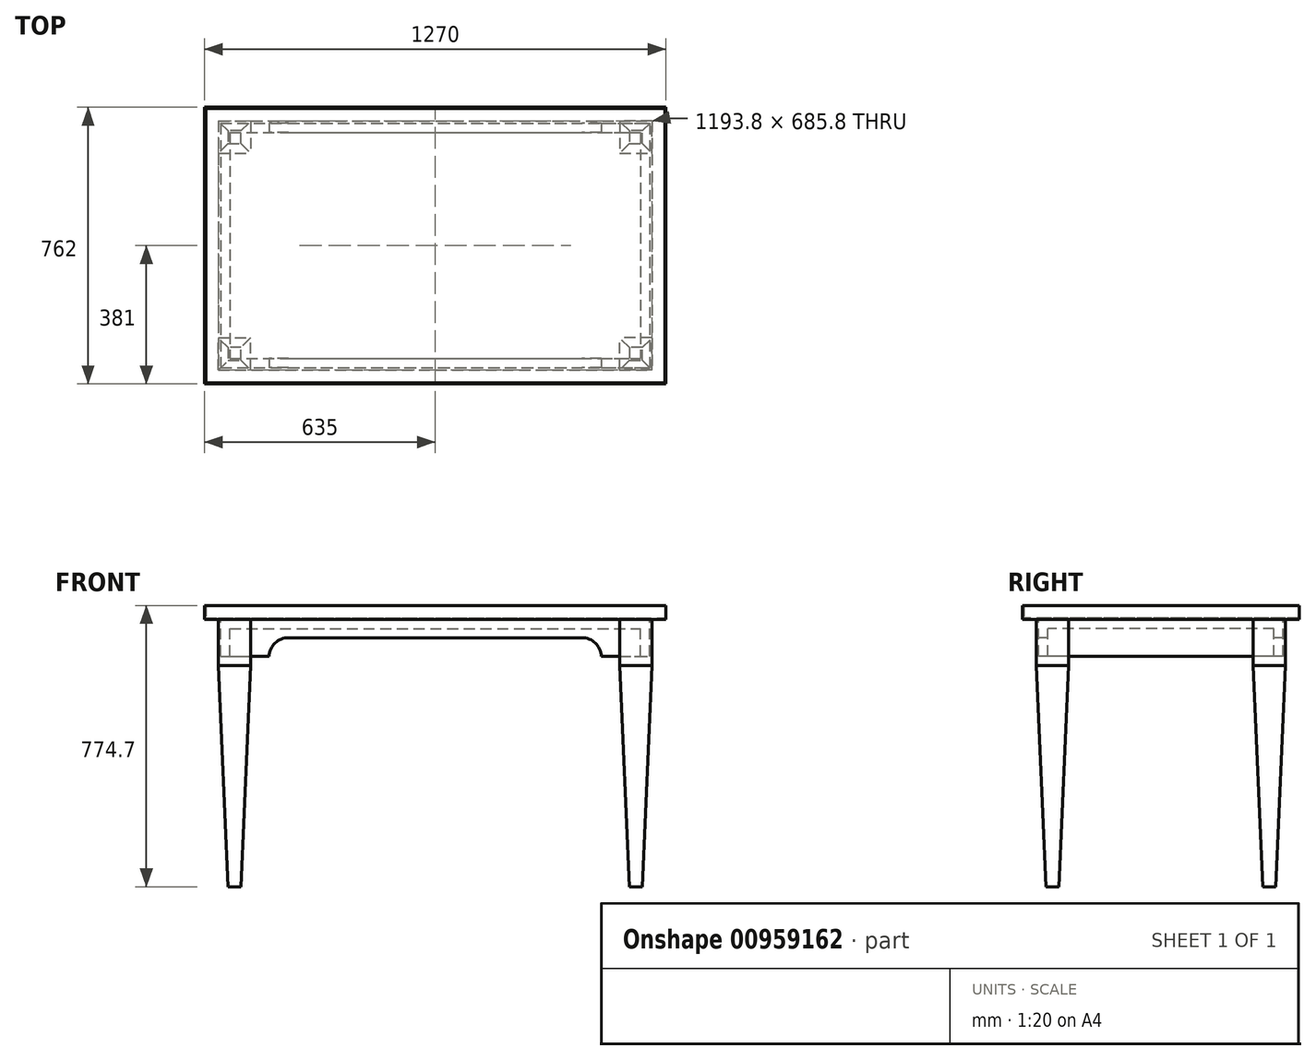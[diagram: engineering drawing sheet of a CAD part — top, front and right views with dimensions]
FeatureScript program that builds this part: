
annotation { "Feature Type Name" : "Feature", "Feature Type Description" : "" }
export const myFeature = defineFeature(function(context is Context, id is Id, definition is map)
    precondition{}
    {
        {
            var Q0;
            Q0=qCreatedBy(makeId("Top.planeOp"),FACE);
            var sketch = newSketch(context, id + "F0", { "sketchPlane" : qUnion([Q0])});
            skLineSegment(sketch, "E0.bottom", {"start": v(-635, 381) * mm, "end": v(635, 381) * mm});
            skLineSegment(sketch, "E0.top", {"start": v(-635, -381) * mm, "end": v(635, -381) * mm});
            skLineSegment(sketch, "E0.left", {"start": v(-635, 381) * mm, "end": v(-635, -381) * mm});
            skLineSegment(sketch, "E0.right", {"start": v(635, 381) * mm, "end": v(635, -381) * mm});
            skPoint(sketch, "E0.middle", {"position": v(0, 0) * mm});
            skLineSegment(sketch, "E1.0", {"start": v(-631.82, 377.83) * mm, "end": v(631.83, 377.83) * mm});
            skLineSegment(sketch, "E1.1", {"start": v(-631.82, 377.83) * mm, "end": v(-631.83, -377.82) * mm});
            skLineSegment(sketch, "E1.2", {"start": v(-631.83, -377.82) * mm, "end": v(631.82, -377.82) * mm});
            skLineSegment(sketch, "E1.3", {"start": v(631.83, 377.83) * mm, "end": v(631.82, -377.82) * mm});
            skLineSegment(sketch, "E2.0", {"start": v(-596.9, 342.9) * mm, "end": v(596.9, 342.9) * mm});
            skLineSegment(sketch, "E2.1", {"start": v(-596.9, 342.9) * mm, "end": v(-596.9, -342.9) * mm});
            skLineSegment(sketch, "E2.2", {"start": v(-596.9, -342.9) * mm, "end": v(596.9, -342.9) * mm});
            skLineSegment(sketch, "E2.3", {"start": v(596.9, 342.9) * mm, "end": v(596.9, -342.9) * mm});
            skSolve(sketch);
        }
        {
            var Q0;
            Q0=qSketchRegion(id+"F0",true);
            extrude(context, id + "F1", {"entities" : qUnion([Q0]), "depth" : 38.1 * mm, "offsetDistance" : 25.4 * mm});
        }
        {
            var Q0;
            Q0=makeQuery(id+"F1.opExtrude","CAP_FACE",FACE,{"disambiguationData":[OSD([sQuery(id+"F0.wireOp",EDGE,"E0.bottom"),sQuery(id+"F0.wireOp",EDGE,"E0.top"),sQuery(id+"F0.wireOp",EDGE,"E0.left"),sQuery(id+"F0.wireOp",EDGE,"E0.right")])],"isStart":true});
            var sketch = newSketch(context, id + "F2", { "sketchPlane" : qUnion([Q0])});
            skLineSegment(sketch, "E3.bottom", {"start": v(-635, -381) * mm, "end": v(635, -381) * mm});
            skLineSegment(sketch, "E3.top", {"start": v(-635, 381) * mm, "end": v(635, 381) * mm});
            skLineSegment(sketch, "E3.left", {"start": v(-635, -381) * mm, "end": v(-635, 381) * mm});
            skLineSegment(sketch, "E3.right", {"start": v(635, -381) * mm, "end": v(635, 381) * mm});
            skPoint(sketch, "E3.middle", {"position": v(0, 0) * mm});
            skLineSegment(sketch, "E4.0", {"start": v(-596.9, -342.9) * mm, "end": v(-596.9, 342.9) * mm});
            skLineSegment(sketch, "E4.1", {"start": v(-596.9, -342.9) * mm, "end": v(596.9, -342.9) * mm});
            skLineSegment(sketch, "E4.2", {"start": v(596.9, -342.9) * mm, "end": v(596.9, 342.9) * mm});
            skLineSegment(sketch, "E4.3", {"start": v(-596.9, 342.9) * mm, "end": v(596.9, 342.9) * mm});
            skLineSegment(sketch, "E5.0", {"start": v(-590.55, 336.55) * mm, "end": v(590.55, 336.55) * mm});
            skLineSegment(sketch, "E5.1", {"start": v(-590.55, -336.55) * mm, "end": v(-590.55, 336.55) * mm});
            skLineSegment(sketch, "E5.2", {"start": v(-590.55, -336.55) * mm, "end": v(590.55, -336.55) * mm});
            skLineSegment(sketch, "E5.3", {"start": v(590.55, -336.55) * mm, "end": v(590.55, 336.55) * mm});
            skLineSegment(sketch, "E6.bottom", {"start": v(-596.9, 342.9) * mm, "end": v(-508, 342.9) * mm});
            skLineSegment(sketch, "E6.top", {"start": v(-596.9, 254) * mm, "end": v(-508, 254) * mm});
            skLineSegment(sketch, "E6.left", {"start": v(-596.9, 342.9) * mm, "end": v(-596.9, 254) * mm});
            skLineSegment(sketch, "E6.right", {"start": v(-508, 342.9) * mm, "end": v(-508, 254) * mm});
            skLineSegment(sketch, "E7", {"start": v(-775.87, 0) * mm, "end": v(783.48, 0) * mm, "construction": true});
            skLineSegment(sketch, "E8", {"start": v(0, 524.15) * mm, "end": v(0, -552.6) * mm, "construction": true});
            skLineSegment(sketch, "E9.MirrorCS", {"start": v(-508, -342.9) * mm, "end": v(-508, -254) * mm});
            skLineSegment(sketch, "E10.MirrorCS", {"start": v(-596.9, -342.9) * mm, "end": v(-508, -342.9) * mm});
            skLineSegment(sketch, "E11.MirrorCS", {"start": v(-596.9, -342.9) * mm, "end": v(-596.9, -254) * mm});
            skLineSegment(sketch, "E12.MirrorCS", {"start": v(-596.9, -254) * mm, "end": v(-508, -254) * mm});
            skSolve(sketch);
        }
        {
            var Q0;
            {var subQ0=sQuery(id+"F2.wireOp",EDGE,"E5.3");Q0=makeQuery(id+"F2.imprint","IMPRINT",FACE,{"disambiguationData":[TD([[makeQuery(id+"F2.imprint","IMPRINT",EDGE,{"derivedFrom":subQ0}),1.0]])]});}
            var sketch = newSketch(context, id + "F3", { "sketchPlane" : qUnion([Q0])});
            skLineSegment(sketch, "E13.0", {"start": v(-596.9, 342.9) * mm, "end": v(-508, 342.9) * mm});
            skLineSegment(sketch, "E14.0", {"start": v(-508, 342.9) * mm, "end": v(-508, 254) * mm});
            skLineSegment(sketch, "E15.0", {"start": v(-596.9, 342.9) * mm, "end": v(-596.9, 254) * mm});
            skLineSegment(sketch, "E16.0", {"start": v(-596.9, 254) * mm, "end": v(-508, 254) * mm});
            skLineSegment(sketch, "E17.0", {"start": v(-596.9, -254) * mm, "end": v(-508, -254) * mm});
            skLineSegment(sketch, "E18.0", {"start": v(-508, -342.9) * mm, "end": v(-508, -254) * mm});
            skLineSegment(sketch, "E19.0", {"start": v(-596.9, -342.9) * mm, "end": v(-508, -342.9) * mm});
            skLineSegment(sketch, "E20.0", {"start": v(-596.9, -342.9) * mm, "end": v(-596.9, -254) * mm});
            skSolve(sketch);
        }
        {
            var Q0;
            Q0=qSketchRegion(id+"F3",true);
            extrude(context, id + "F4", {"entities" : qUnion([Q0]), "depth" : 127 * mm, "offsetDistance" : 25.4 * mm});
        }
        {
            var Q0;
            Q0=makeQuery(id+"F4.opExtrude","SWEPT_BODY",BODY,{"disambiguationData":[OSD([sQuery(id+"F3.wireOp",EDGE,"E13.0"),sQuery(id+"F3.wireOp",EDGE,"E14.0"),sQuery(id+"F3.wireOp",EDGE,"E15.0"),sQuery(id+"F3.wireOp",EDGE,"E16.0")])]});
            var Q1;
            Q1=makeQuery(id+"F4.opExtrude","SWEPT_BODY",BODY,{"disambiguationData":[OSD([sQuery(id+"F3.wireOp",EDGE,"E17.0"),sQuery(id+"F3.wireOp",EDGE,"E18.0"),sQuery(id+"F3.wireOp",EDGE,"E19.0"),sQuery(id+"F3.wireOp",EDGE,"E20.0")])]});
            var Q2;
            Q2=qCreatedBy(makeId("Right.planeOp"),FACE);
            mirror(context, id + "F5", {"operationType" : NewBodyOperationType.ADD, "entities" : qUnion([Q0, Q1]), "mirrorPlane" : qUnion([Q2])});
        }
        {
            var Q0;
            {var subQ0=sQuery(id+"F2.wireOp",EDGE,"E5.3");Q0=makeQuery(id+"F2.imprint","IMPRINT",FACE,{"disambiguationData":[TD([[makeQuery(id+"F2.imprint","IMPRINT",EDGE,{"derivedFrom":subQ0}),1.0]])]});}
            var sketch = newSketch(context, id + "F6", { "sketchPlane" : qUnion([Q0])});
            skLineSegment(sketch, "E21.0", {"start": v(-590.55, 336.55) * mm, "end": v(590.55, 336.55) * mm});
            skLineSegment(sketch, "E22.0", {"start": v(-590.55, -336.55) * mm, "end": v(-590.55, 336.55) * mm});
            skLineSegment(sketch, "E23.0", {"start": v(-590.55, -336.55) * mm, "end": v(590.55, -336.55) * mm});
            skLineSegment(sketch, "E24.0", {"start": v(590.55, -336.55) * mm, "end": v(590.55, 336.55) * mm});
            skSolve(sketch);
        }
        {
            var Q0;
            Q0=qSketchRegion(id+"F6",true);
            extrude(context, id + "F7", {"entities" : qUnion([Q0]), "depth" : 101.6 * mm, "offsetDistance" : 25.4 * mm});
        }
        {
            var Q0;
            Q0=makeQuery(id+"F7.opExtrude","CAP_FACE",FACE,{"disambiguationData":[OSD([sQuery(id+"F6.wireOp",EDGE,"E21.0"),sQuery(id+"F6.wireOp",EDGE,"E22.0"),sQuery(id+"F6.wireOp",EDGE,"E23.0"),sQuery(id+"F6.wireOp",EDGE,"E24.0")])],"isStart":false});
            var Q1;
            Q1=makeQuery(id+"F7.opExtrude","SWEPT_BODY",BODY,{"disambiguationData":[OSD([sQuery(id+"F6.wireOp",EDGE,"E21.0"),sQuery(id+"F6.wireOp",EDGE,"E22.0"),sQuery(id+"F6.wireOp",EDGE,"E23.0"),sQuery(id+"F6.wireOp",EDGE,"E24.0")])]});
            shell(context, id + "F8", {"entities" : qUnion([Q0]), "parts" : qUnion([Q1]), "thickness" : 25.4 * mm});
        }
        {
            var Q0;
            Q0=qCreatedBy(makeId("Top.planeOp"),FACE);
            var sketch = newSketch(context, id + "F9", { "sketchPlane" : qUnion([Q0])});
            skLineSegment(sketch, "E25.0", {"start": v(-596.9, 342.9) * mm, "end": v(596.9, 342.9) * mm});
            skLineSegment(sketch, "E26.0", {"start": v(-596.9, 342.9) * mm, "end": v(-596.9, -342.9) * mm});
            skLineSegment(sketch, "E27.0", {"start": v(-596.9, -342.9) * mm, "end": v(596.9, -342.9) * mm});
            skLineSegment(sketch, "E28.0", {"start": v(596.9, 342.9) * mm, "end": v(596.9, -342.9) * mm});
            skLineSegment(sketch, "E29.0", {"start": v(-635, 381) * mm, "end": v(635, 381) * mm});
            skLineSegment(sketch, "E30.0", {"start": v(-635, 381) * mm, "end": v(-635, -381) * mm});
            skLineSegment(sketch, "E31.0", {"start": v(-635, -381) * mm, "end": v(635, -381) * mm});
            skLineSegment(sketch, "E32.0", {"start": v(635, 381) * mm, "end": v(635, -381) * mm});
            skSolve(sketch);
        }
        {
            var Q0;
            Q0=qSketchRegion(id+"F9",true);
            extrude(context, id + "F10", {"entities" : qUnion([Q0]), "operationType" : NewBodyOperationType.ADD, "depth" : 3.17 * mm, "offsetDistance" : 25.4 * mm});
        }
        {
            var Q0;
            Q0=qCreatedBy(makeId("Top.planeOp"),FACE);
            var sketch = newSketch(context, id + "F11", { "sketchPlane" : qUnion([Q0])});
            skLineSegment(sketch, "E33.0", {"start": v(-635, 381) * mm, "end": v(635, 381) * mm});
            skLineSegment(sketch, "E34.0", {"start": v(-635, 381) * mm, "end": v(-635, -381) * mm});
            skLineSegment(sketch, "E35.0", {"start": v(-635, -381) * mm, "end": v(635, -381) * mm});
            skLineSegment(sketch, "E36.0", {"start": v(635, 381) * mm, "end": v(635, -381) * mm});
            skSolve(sketch);
        }
        {
            var Q0;
            Q0=qSketchRegion(id+"F11",true);
            extrude(context, id + "F12", {"entities" : qUnion([Q0]), "depth" : 38.1 * mm, "offsetDistance" : 25.4 * mm});
        }
        {
            var Q0;
            Q0=makeQuery(id+"F4.opExtrude","CAP_FACE",FACE,{"disambiguationData":[OSD([sQuery(id+"F3.wireOp",EDGE,"E13.0"),sQuery(id+"F3.wireOp",EDGE,"E14.0"),sQuery(id+"F3.wireOp",EDGE,"E15.0"),sQuery(id+"F3.wireOp",EDGE,"E16.0")])],"isStart":false});
            var sketch = newSketch(context, id + "F13", { "sketchPlane" : qUnion([Q0])});
            skLineSegment(sketch, "E37.0.0", {"start": v(-596.9, 342.9) * mm, "end": v(-596.9, 254) * mm});
            skLineSegment(sketch, "E37.0.1", {"start": v(-596.9, 254) * mm, "end": v(-508, 254) * mm});
            skLineSegment(sketch, "E37.0.2", {"start": v(-508, 254) * mm, "end": v(-508, 342.9) * mm});
            skLineSegment(sketch, "E37.0.3", {"start": v(-508, 342.9) * mm, "end": v(-596.9, 342.9) * mm});
            skLineSegment(sketch, "E38.0.0", {"start": v(596.9, 254) * mm, "end": v(596.9, 342.9) * mm});
            skLineSegment(sketch, "E38.0.1", {"start": v(596.9, 342.9) * mm, "end": v(508, 342.9) * mm});
            skLineSegment(sketch, "E38.0.2", {"start": v(508, 342.9) * mm, "end": v(508, 254) * mm});
            skLineSegment(sketch, "E38.0.3", {"start": v(508, 254) * mm, "end": v(596.9, 254) * mm});
            skLineSegment(sketch, "E39.0.0", {"start": v(508, -342.9) * mm, "end": v(596.9, -342.9) * mm});
            skLineSegment(sketch, "E39.0.1", {"start": v(596.9, -342.9) * mm, "end": v(596.9, -254) * mm});
            skLineSegment(sketch, "E39.0.2", {"start": v(596.9, -254) * mm, "end": v(508, -254) * mm});
            skLineSegment(sketch, "E39.0.3", {"start": v(508, -254) * mm, "end": v(508, -342.9) * mm});
            skLineSegment(sketch, "E40.0.0", {"start": v(-596.9, -342.9) * mm, "end": v(-508, -342.9) * mm});
            skLineSegment(sketch, "E40.0.1", {"start": v(-508, -342.9) * mm, "end": v(-508, -254) * mm});
            skLineSegment(sketch, "E40.0.2", {"start": v(-508, -254) * mm, "end": v(-596.9, -254) * mm});
            skLineSegment(sketch, "E40.0.3", {"start": v(-596.9, -254) * mm, "end": v(-596.9, -342.9) * mm});
            skSolve(sketch);
        }
        {
            var Q0;
            Q0=qSketchRegion(id+"F13",true);
            extrude(context, id + "F14", {"entities" : qUnion([Q0]), "depth" : 609.6 * mm, "offsetDistance" : 25.4 * mm, "hasDraft" : true, "draftAngle" : 2.5 * degree, "draftPullDirection" : true});
        }
        {
            var Q0;
            Q0=makeQuery(id+"F7.opExtrude","SWEPT_FACE",FACE,{"disambiguationData":[OSD([sQuery(id+"F6.wireOp",EDGE,"E21.0")])]});
            var sketch = newSketch(context, id + "F15", { "sketchPlane" : qUnion([Q0])});
            skLineSegment(sketch, "E41.0.0", {"start": v(590.55, 0) * mm, "end": v(-590.55, 0) * mm, "construction": true});
            skLineSegment(sketch, "E41.0.1", {"start": v(-590.55, 0) * mm, "end": v(-590.55, -101.6) * mm, "construction": true});
            skLineSegment(sketch, "E41.0.2", {"start": v(-590.55, -101.6) * mm, "end": v(590.55, -101.6) * mm, "construction": true});
            skLineSegment(sketch, "E41.0.3", {"start": v(590.55, -101.6) * mm, "end": v(590.55, 0) * mm, "construction": true});
            skLineSegment(sketch, "E42.0.0", {"start": v(-508, 0) * mm, "end": v(-596.9, 0) * mm, "construction": true});
            skLineSegment(sketch, "E42.0.1", {"start": v(-596.9, 0) * mm, "end": v(-596.9, -127) * mm, "construction": true});
            skLineSegment(sketch, "E42.0.2", {"start": v(-596.9, -127) * mm, "end": v(-508, -127) * mm, "construction": true});
            skLineSegment(sketch, "E42.0.3", {"start": v(-508, -127) * mm, "end": v(-508, 0) * mm, "construction": true});
            skLineSegment(sketch, "E43", {"start": v(-508, -101.6) * mm, "end": v(-457.2, -101.6) * mm, "construction": true});
            skLineSegment(sketch, "E44", {"start": v(0, 0) * mm, "end": v(0, -222.96) * mm, "construction": true});
            skLineSegment(sketch, "E45", {"start": v(0, -222.96) * mm, "end": v(0, -50.8) * mm, "construction": true});
            skLineSegment(sketch, "E46", {"start": v(0, -50.8) * mm, "end": v(-404.04, -50.8) * mm, "construction": true});
            skLineSegment(sketch, "E47.MirrorCS", {"start": v(0, 121.36) * mm, "end": v(0, -50.8) * mm, "construction": true});
            skLineSegment(sketch, "E48.MirrorCS", {"start": v(0, -50.8) * mm, "end": v(404.04, -50.8) * mm, "construction": true});
            skArc(sketch, "E49", {"start": v(-404.04, -50.8) * mm, "mid": v(-440.8, -65.54) * mm, "end": v(-457.2, -101.6) * mm});
            skArc(sketch, "E50.MirrorCS", {"start": v(404.04, -50.8) * mm, "mid": v(440.8, -65.54) * mm, "end": v(457.2, -101.6) * mm});
            skLineSegment(sketch, "E51", {"start": v(-404.04, -50.8) * mm, "end": v(404.04, -50.8) * mm});
            skLineSegment(sketch, "E52.bottom", {"start": v(-457.2, -101.6) * mm, "end": v(457.2, -101.6) * mm});
            skLineSegment(sketch, "E52.top", {"start": v(-457.2, -191.58) * mm, "end": v(457.2, -191.58) * mm});
            skLineSegment(sketch, "E52.left", {"start": v(-457.2, -101.6) * mm, "end": v(-457.2, -191.58) * mm});
            skLineSegment(sketch, "E52.right", {"start": v(457.2, -101.6) * mm, "end": v(457.2, -191.58) * mm});
            skSolve(sketch);
        }
        {
            var Q0;
            Q0=qSketchRegion(id+"F15",true);
            extrude(context, id + "F16", {"entities" : qUnion([Q0]), "operationType" : NewBodyOperationType.REMOVE, "oppositeDirection" : true, "depth" : 1219.2 * mm, "offsetDistance" : 25.4 * mm});
        }
    });
